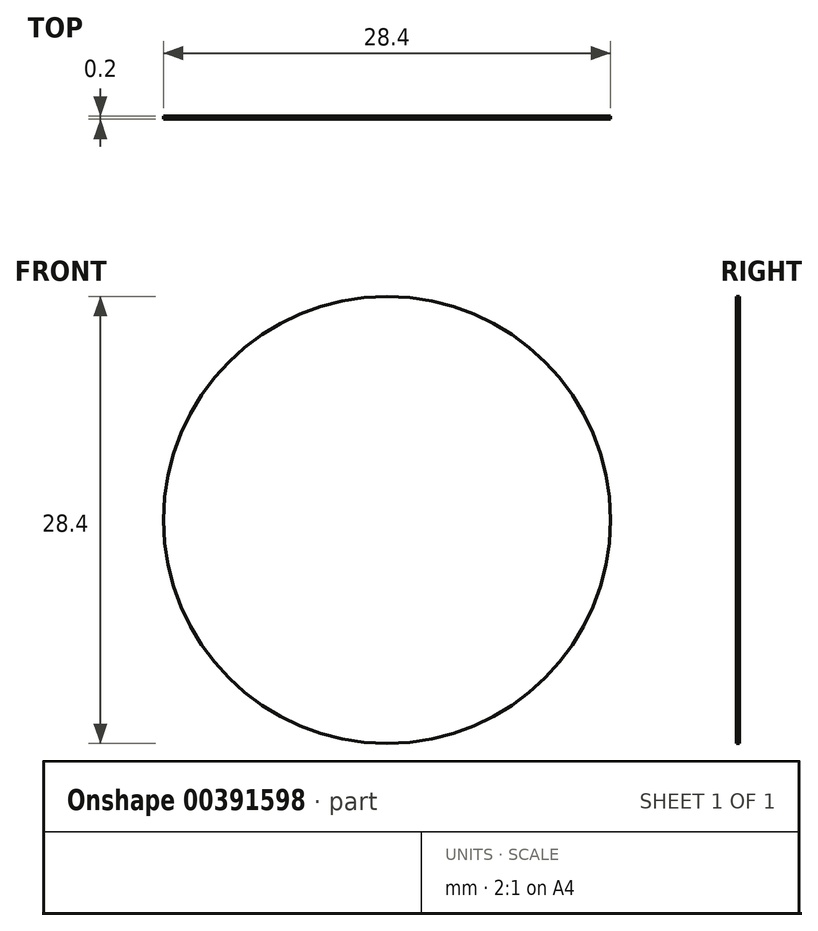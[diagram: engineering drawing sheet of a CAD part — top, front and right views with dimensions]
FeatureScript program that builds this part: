
annotation { "Feature Type Name" : "Feature", "Feature Type Description" : "" }
export const myFeature = defineFeature(function(context is Context, id is Id, definition is map)
    precondition{}
    {
        {
            var Q0;
            Q0=qCreatedBy(makeId("Front.planeOp"),FACE);
            var sketch = newSketch(context, id + "F0", { "sketchPlane" : qUnion([Q0])});
            skCircle(sketch, "E0", {"center": v(0, 0) * mm, "radius": 7 * mm, "construction": true});
            skCircle(sketch, "E1", {"center": v(0, 0) * mm, "radius": 10.5 * mm, "construction": true});
            skLineSegment(sketch, "E2", {"start": v(0, 7) * mm, "end": v(0.75, 7) * mm, "construction": true});
            skLineSegment(sketch, "E3", {"start": v(0.75, 7) * mm, "end": v(0.75, 13.5) * mm, "construction": true});
            skLineSegment(sketch, "E4", {"start": v(0.75, 13.5) * mm, "end": v(0, 13.5) * mm, "construction": true});
            skLineSegment(sketch, "E5", {"start": v(0, 13.5) * mm, "end": v(-0.75, 13.5) * mm, "construction": true});
            skLineSegment(sketch, "E6", {"start": v(-0.75, 13.5) * mm, "end": v(-0.75, 7) * mm, "construction": true});
            skLineSegment(sketch, "E7", {"start": v(-0.75, 7) * mm, "end": v(0, 7) * mm, "construction": true});
            skLineSegment(sketch, "E8.1.0", {"start": v(-2.85, 6.44) * mm, "end": v(-6.1, 12.07) * mm});
            skLineSegment(sketch, "E8.1.1", {"start": v(-7.4, 11.32) * mm, "end": v(-4.15, 5.69) * mm});
            skLineSegment(sketch, "E8.1.2", {"start": v(-4.15, 5.69) * mm, "end": v(-3.5, 6.06) * mm});
            skLineSegment(sketch, "E8.1.3", {"start": v(-3.5, 6.06) * mm, "end": v(-2.85, 6.44) * mm});
            skLineSegment(sketch, "E8.1.4", {"start": v(-6.1, 12.07) * mm, "end": v(-6.75, 11.7) * mm});
            skLineSegment(sketch, "E8.1.5", {"start": v(-6.75, 11.7) * mm, "end": v(-7.4, 11.32) * mm});
            skLineSegment(sketch, "E8.2.0", {"start": v(-5.69, 4.15) * mm, "end": v(-11.32, 7.4) * mm});
            skLineSegment(sketch, "E8.2.1", {"start": v(-12.07, 6.1) * mm, "end": v(-6.44, 2.85) * mm});
            skLineSegment(sketch, "E8.2.2", {"start": v(-6.44, 2.85) * mm, "end": v(-6.06, 3.5) * mm});
            skLineSegment(sketch, "E8.2.3", {"start": v(-6.06, 3.5) * mm, "end": v(-5.69, 4.15) * mm});
            skLineSegment(sketch, "E8.2.4", {"start": v(-11.32, 7.4) * mm, "end": v(-11.7, 6.75) * mm});
            skLineSegment(sketch, "E8.2.5", {"start": v(-11.7, 6.75) * mm, "end": v(-12.07, 6.1) * mm});
            skLineSegment(sketch, "E8.3.0", {"start": v(-7, 0.75) * mm, "end": v(-13.5, 0.75) * mm, "construction": true});
            skLineSegment(sketch, "E8.3.1", {"start": v(-13.5, -0.75) * mm, "end": v(-7, -0.75) * mm, "construction": true});
            skLineSegment(sketch, "E8.3.2", {"start": v(-7, -0.75) * mm, "end": v(-7, 0) * mm, "construction": true});
            skLineSegment(sketch, "E8.3.3", {"start": v(-7, 0) * mm, "end": v(-7, 0.75) * mm, "construction": true});
            skLineSegment(sketch, "E8.3.4", {"start": v(-13.5, 0.75) * mm, "end": v(-13.5, 0) * mm, "construction": true});
            skLineSegment(sketch, "E8.3.5", {"start": v(-13.5, 0) * mm, "end": v(-13.5, -0.75) * mm, "construction": true});
            skLineSegment(sketch, "E8.4.0", {"start": v(-6.44, -2.85) * mm, "end": v(-12.07, -6.1) * mm});
            skLineSegment(sketch, "E8.4.1", {"start": v(-11.32, -7.4) * mm, "end": v(-5.69, -4.15) * mm});
            skLineSegment(sketch, "E8.4.2", {"start": v(-5.69, -4.15) * mm, "end": v(-6.06, -3.5) * mm});
            skLineSegment(sketch, "E8.4.3", {"start": v(-6.06, -3.5) * mm, "end": v(-6.44, -2.85) * mm});
            skLineSegment(sketch, "E8.4.4", {"start": v(-12.07, -6.1) * mm, "end": v(-11.7, -6.75) * mm});
            skLineSegment(sketch, "E8.4.5", {"start": v(-11.7, -6.75) * mm, "end": v(-11.32, -7.4) * mm});
            skLineSegment(sketch, "E8.5.0", {"start": v(-4.15, -5.69) * mm, "end": v(-7.4, -11.32) * mm});
            skLineSegment(sketch, "E8.5.1", {"start": v(-6.1, -12.07) * mm, "end": v(-2.85, -6.44) * mm});
            skLineSegment(sketch, "E8.5.2", {"start": v(-2.85, -6.44) * mm, "end": v(-3.5, -6.06) * mm});
            skLineSegment(sketch, "E8.5.3", {"start": v(-3.5, -6.06) * mm, "end": v(-4.15, -5.69) * mm});
            skLineSegment(sketch, "E8.5.4", {"start": v(-7.4, -11.32) * mm, "end": v(-6.75, -11.7) * mm});
            skLineSegment(sketch, "E8.5.5", {"start": v(-6.75, -11.7) * mm, "end": v(-6.1, -12.07) * mm});
            skLineSegment(sketch, "E8.6.0", {"start": v(-0.75, -7) * mm, "end": v(-0.75, -13.5) * mm, "construction": true});
            skLineSegment(sketch, "E8.6.1", {"start": v(0.75, -13.5) * mm, "end": v(0.75, -7) * mm, "construction": true});
            skLineSegment(sketch, "E8.6.2", {"start": v(0.75, -7) * mm, "end": v(0, -7) * mm, "construction": true});
            skLineSegment(sketch, "E8.6.3", {"start": v(0, -7) * mm, "end": v(-0.75, -7) * mm, "construction": true});
            skLineSegment(sketch, "E8.6.4", {"start": v(-0.75, -13.5) * mm, "end": v(0, -13.5) * mm, "construction": true});
            skLineSegment(sketch, "E8.6.5", {"start": v(0, -13.5) * mm, "end": v(0.75, -13.5) * mm, "construction": true});
            skLineSegment(sketch, "E8.7.0", {"start": v(2.85, -6.44) * mm, "end": v(6.1, -12.07) * mm});
            skLineSegment(sketch, "E8.7.1", {"start": v(7.4, -11.32) * mm, "end": v(4.15, -5.69) * mm});
            skLineSegment(sketch, "E8.7.2", {"start": v(4.15, -5.69) * mm, "end": v(3.5, -6.06) * mm});
            skLineSegment(sketch, "E8.7.3", {"start": v(3.5, -6.06) * mm, "end": v(2.85, -6.44) * mm});
            skLineSegment(sketch, "E8.7.4", {"start": v(6.1, -12.07) * mm, "end": v(6.75, -11.7) * mm});
            skLineSegment(sketch, "E8.7.5", {"start": v(6.75, -11.7) * mm, "end": v(7.4, -11.32) * mm});
            skLineSegment(sketch, "E8.8.0", {"start": v(5.69, -4.15) * mm, "end": v(11.32, -7.4) * mm});
            skLineSegment(sketch, "E8.8.1", {"start": v(12.07, -6.1) * mm, "end": v(6.44, -2.85) * mm});
            skLineSegment(sketch, "E8.8.2", {"start": v(6.44, -2.85) * mm, "end": v(6.06, -3.5) * mm});
            skLineSegment(sketch, "E8.8.3", {"start": v(6.06, -3.5) * mm, "end": v(5.69, -4.15) * mm});
            skLineSegment(sketch, "E8.8.4", {"start": v(11.32, -7.4) * mm, "end": v(11.7, -6.75) * mm});
            skLineSegment(sketch, "E8.8.5", {"start": v(11.7, -6.75) * mm, "end": v(12.07, -6.1) * mm});
            skLineSegment(sketch, "E8.9.0", {"start": v(7, -0.75) * mm, "end": v(13.5, -0.75) * mm, "construction": true});
            skLineSegment(sketch, "E8.9.1", {"start": v(13.5, 0.75) * mm, "end": v(7, 0.75) * mm, "construction": true});
            skLineSegment(sketch, "E8.9.2", {"start": v(7, 0.75) * mm, "end": v(7, 0) * mm, "construction": true});
            skLineSegment(sketch, "E8.9.3", {"start": v(7, 0) * mm, "end": v(7, -0.75) * mm, "construction": true});
            skLineSegment(sketch, "E8.9.4", {"start": v(13.5, -0.75) * mm, "end": v(13.5, 0) * mm, "construction": true});
            skLineSegment(sketch, "E8.9.5", {"start": v(13.5, 0) * mm, "end": v(13.5, 0.75) * mm, "construction": true});
            skLineSegment(sketch, "E8.10.0", {"start": v(6.44, 2.85) * mm, "end": v(12.07, 6.1) * mm});
            skLineSegment(sketch, "E8.10.1", {"start": v(11.32, 7.4) * mm, "end": v(5.69, 4.15) * mm});
            skLineSegment(sketch, "E8.10.2", {"start": v(5.69, 4.15) * mm, "end": v(6.06, 3.5) * mm});
            skLineSegment(sketch, "E8.10.3", {"start": v(6.06, 3.5) * mm, "end": v(6.44, 2.85) * mm});
            skLineSegment(sketch, "E8.10.4", {"start": v(12.07, 6.1) * mm, "end": v(11.7, 6.75) * mm});
            skLineSegment(sketch, "E8.10.5", {"start": v(11.7, 6.75) * mm, "end": v(11.32, 7.4) * mm});
            skLineSegment(sketch, "E8.11.0", {"start": v(4.15, 5.69) * mm, "end": v(7.4, 11.32) * mm});
            skLineSegment(sketch, "E8.11.1", {"start": v(6.1, 12.07) * mm, "end": v(2.85, 6.44) * mm});
            skLineSegment(sketch, "E8.11.2", {"start": v(2.85, 6.44) * mm, "end": v(3.5, 6.06) * mm});
            skLineSegment(sketch, "E8.11.3", {"start": v(3.5, 6.06) * mm, "end": v(4.15, 5.69) * mm});
            skLineSegment(sketch, "E8.11.4", {"start": v(7.4, 11.32) * mm, "end": v(6.75, 11.7) * mm});
            skLineSegment(sketch, "E8.11.5", {"start": v(6.75, 11.7) * mm, "end": v(6.1, 12.07) * mm});
            skCircle(sketch, "E9", {"center": v(0, 0) * mm, "radius": 13.5 * mm, "construction": true});
            skSolve(sketch);
        }
        {
            var Q0;
            Q0=qCreatedBy(makeId("Front.planeOp"),FACE);
            var sketch = newSketch(context, id + "F1", { "sketchPlane" : qUnion([Q0])});
            skText(sketch, "E10", { "text": "12", "fontName": "AllertaStencil-Regular.ttf"});
            skText(sketch, "E11", { "text": "6", "fontName": "AllertaStencil-Regular.ttf"});
            skText(sketch, "E12", { "text": "9", "fontName": "AllertaStencil-Regular.ttf"});
            skPoint(sketch, "E13", {"position": v(-13.5, 0) * mm});
            skText(sketch, "E14", { "text": "3", "fontName": "AllertaStencil-Regular.ttf"});
            skCircle(sketch, "E15", {"center": v(0, 0) * mm, "radius": 13.5 * mm, "construction": true});
            skCircle(sketch, "E16", {"center": v(0, 0) * mm, "radius": 10 * mm, "construction": true});
            skLineSegment(sketch, "E17", {"start": v(0, 0) * mm, "end": v(0, 13.5) * mm, "construction": true});
            skLineSegment(sketch, "E18.1.0", {"start": v(0, 0) * mm, "end": v(-13.5, 0) * mm, "construction": true});
            skLineSegment(sketch, "E18.2.0", {"start": v(0, 0) * mm, "end": v(0, -13.5) * mm, "construction": true});
            skLineSegment(sketch, "E18.3.0", {"start": v(0, 0) * mm, "end": v(13.5, 0) * mm, "construction": true});
            skPoint(sketch, "E19", {"position": v(13.5, 0) * mm});
            const initialGuessF1  = {"E10": [-0.00246, 0.01, 1, 0, 0.0035], "E11": [-0.00153, -0.0135, 1, 0, 0.0035], "E12": [-0.0135, -0.00175, 1, 0, 0.0035], "E14": [0.01076, -0.00175, 1, 0, 0.0035]};
            skSetInitialGuess(sketch, initialGuessF1);
            skSolve(sketch);
        }
        {
            var Q0;
            Q0=qCreatedBy(makeId("Front.planeOp"),FACE);
            var sketch = newSketch(context, id + "F2", { "sketchPlane" : qUnion([Q0])});
            skCircle(sketch, "E20", {"center": v(0, 0) * mm, "radius": 14.2 * mm});
            skSolve(sketch);
        }
        {
            var Q0;
            Q0=qCreatedBy(makeId("Front.planeOp"),FACE);
            var sketch = newSketch(context, id + "F3", { "sketchPlane" : qUnion([Q0])});
            skLineSegment(sketch, "E21", {"start": v(-1.79, 9.56) * mm, "end": v(1.79, 9.56) * mm});
            skLineSegment(sketch, "E22", {"start": v(1.79, 9.56) * mm, "end": v(0, 6.46) * mm});
            skLineSegment(sketch, "E23", {"start": v(0, 6.46) * mm, "end": v(-1.79, 9.56) * mm});
            skSolve(sketch);
        }
        {
            var Q0;
            Q0=qCreatedBy(makeId("Front.planeOp"),FACE);
            var sketch = newSketch(context, id + "F4", { "sketchPlane" : qUnion([Q0])});
            skLineSegment(sketch, "E24.bottom", {"start": v(-9.63, -0.91) * mm, "end": v(-6.95, -0.91) * mm});
            skLineSegment(sketch, "E24.top", {"start": v(-9.63, 0.91) * mm, "end": v(-6.95, 0.91) * mm});
            skLineSegment(sketch, "E24.left", {"start": v(-9.63, -0.91) * mm, "end": v(-9.63, 0.91) * mm});
            skLineSegment(sketch, "E24.right", {"start": v(-6.95, -0.91) * mm, "end": v(-6.95, 0.91) * mm});
            skPoint(sketch, "E25", {"position": v(-6.95, 0) * mm});
            skLineSegment(sketch, "E26.1.0", {"start": v(-0.91, -9.63) * mm, "end": v(-0.91, -6.95) * mm});
            skLineSegment(sketch, "E26.1.1", {"start": v(0.91, -9.63) * mm, "end": v(-0.91, -9.63) * mm});
            skLineSegment(sketch, "E26.1.2", {"start": v(0.91, -6.95) * mm, "end": v(-0.91, -6.95) * mm});
            skPoint(sketch, "E26.1.3", {"position": v(0, -6.95) * mm});
            skLineSegment(sketch, "E26.1.4", {"start": v(0.91, -9.63) * mm, "end": v(0.91, -6.95) * mm});
            skLineSegment(sketch, "E26.2.0", {"start": v(9.63, -0.91) * mm, "end": v(6.95, -0.91) * mm});
            skLineSegment(sketch, "E26.2.1", {"start": v(9.63, 0.91) * mm, "end": v(9.63, -0.91) * mm});
            skLineSegment(sketch, "E26.2.2", {"start": v(6.95, 0.91) * mm, "end": v(6.95, -0.91) * mm});
            skPoint(sketch, "E26.2.3", {"position": v(6.95, 0) * mm});
            skLineSegment(sketch, "E26.2.4", {"start": v(9.63, 0.91) * mm, "end": v(6.95, 0.91) * mm});
            skLineSegment(sketch, "E26.3.0", {"start": v(0.91, 9.63) * mm, "end": v(0.91, 6.95) * mm, "construction": true});
            skLineSegment(sketch, "E26.3.1", {"start": v(-0.91, 9.63) * mm, "end": v(0.91, 9.63) * mm, "construction": true});
            skLineSegment(sketch, "E26.3.2", {"start": v(-0.91, 6.95) * mm, "end": v(0.91, 6.95) * mm, "construction": true});
            skPoint(sketch, "E26.3.3", {"position": v(0, 6.95) * mm});
            skLineSegment(sketch, "E26.3.4", {"start": v(-0.91, 9.63) * mm, "end": v(-0.91, 6.95) * mm, "construction": true});
            skPoint(sketch, "E26.center", {"position": v(0, 0) * mm});
            skSolve(sketch);
        }
        {
            var Q0;
            Q0=qSketchRegion(id+"F2",true);
            extrude(context, id + "F5", {"entities" : qUnion([Q0]), "depth" : 0.2 * mm});
        }
    });
